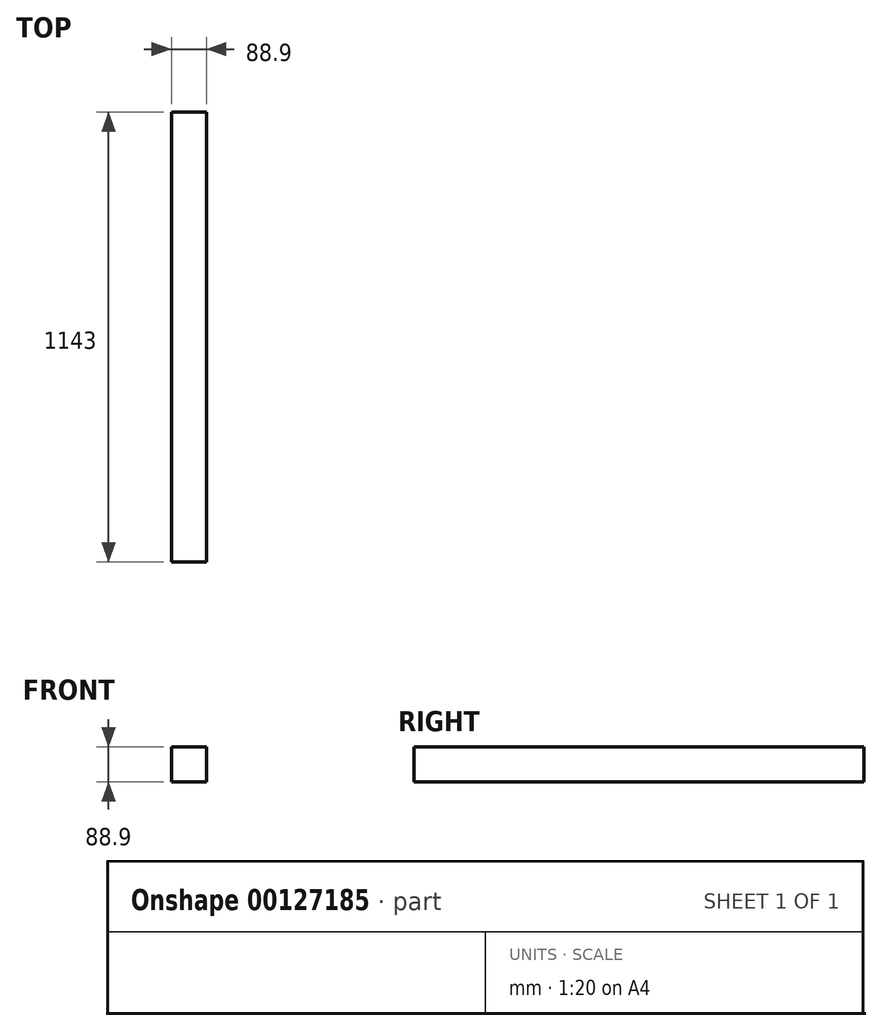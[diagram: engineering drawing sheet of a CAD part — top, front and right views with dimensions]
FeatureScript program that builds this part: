
annotation { "Feature Type Name" : "Feature", "Feature Type Description" : "" }
export const myFeature = defineFeature(function(context is Context, id is Id, definition is map)
    precondition{}
    {
        {
            var Q0;
            Q0=qCreatedBy(makeId("Front.planeOp"),FACE);
            var sketch = newSketch(context, id + "F0", { "sketchPlane" : qUnion([Q0])});
            skLineSegment(sketch, "E0.bottom", {"start": v(44.45, -44.45) * mm, "end": v(-44.45, -44.45) * mm});
            skLineSegment(sketch, "E0.top", {"start": v(44.45, 44.45) * mm, "end": v(-44.45, 44.45) * mm});
            skLineSegment(sketch, "E0.left", {"start": v(44.45, -44.45) * mm, "end": v(44.45, 44.45) * mm});
            skLineSegment(sketch, "E0.right", {"start": v(-44.45, -44.45) * mm, "end": v(-44.45, 44.45) * mm});
            skPoint(sketch, "E0.middle", {"position": v(0, 0) * mm});
            skSolve(sketch);
        }
        {
            var Q0;
            Q0=qSketchRegion(id+"F0",true);
            extrude(context, id + "F1", {"entities" : qUnion([Q0]), "depth" : 1143 * mm});
        }
    });
